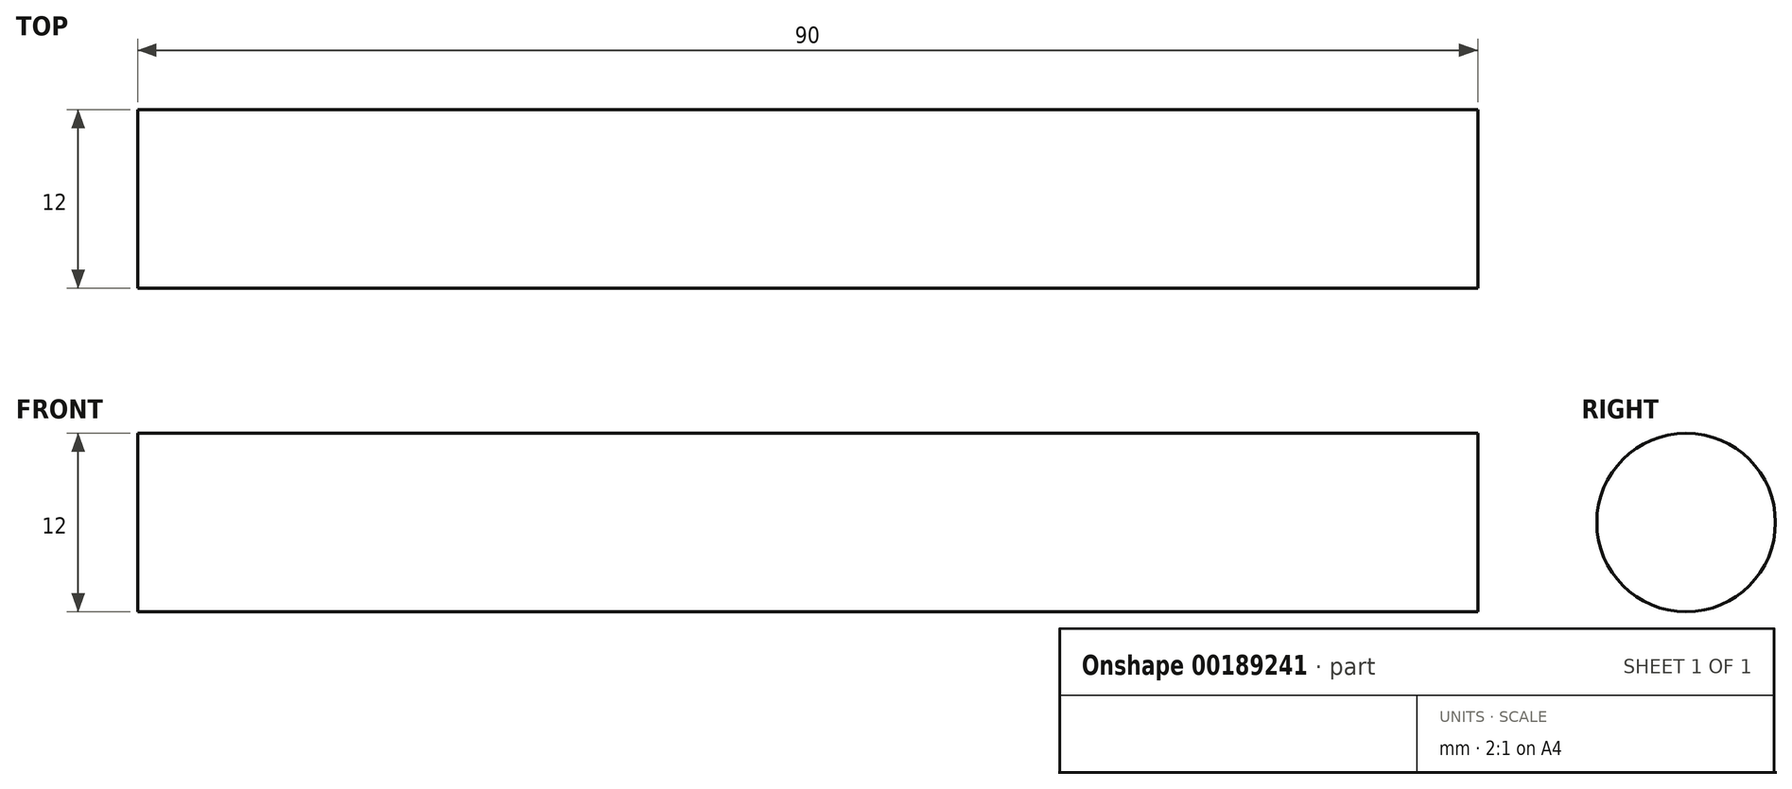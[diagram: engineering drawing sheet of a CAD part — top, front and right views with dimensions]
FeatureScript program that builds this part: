
annotation { "Feature Type Name" : "Feature", "Feature Type Description" : "" }
export const myFeature = defineFeature(function(context is Context, id is Id, definition is map)
    precondition{}
    {
        {
            var Q0;
            Q0=qCreatedBy(makeId("Right.planeOp"),FACE);
            var sketch = newSketch(context, id + "F0", { "sketchPlane" : qUnion([Q0])});
            skCircle(sketch, "E0", {"center": v(0, 0) * mm, "radius": 6 * mm});
            skSolve(sketch);
        }
        {
            var Q0;
            Q0 = qSketchRegion(id + "F0", true);
            extrude(context, id + "F1", {"entities" : qUnion([Q0]), "depth" : 90 * mm});
        }
    });
